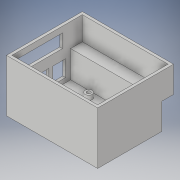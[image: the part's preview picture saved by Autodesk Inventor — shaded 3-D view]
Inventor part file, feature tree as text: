
AUTODESK INVENTOR PART (.ipt)
format: ipt  version: 2019.4 (Build 234330000, 330)  size: 207,872 bytes
history: native  units: mm
features: extrude x7, sketch x7
ambient origin geometry x8: Origin, YZ Plane, XZ Plane, XY Plane, X Axis, Y Axis, Z Axis, Center Point
bodies: Solid1 (feature_tree)
feature tree (14):
  extrude  "Extrusion1"  Depth=65.0mm
  extrude  "Extrusion2"  Depth=32.0mm TaperAngle=0.0deg
  extrude  "Extrusion3"  Depth=65.0mm
  extrude  "Extrusion4"  Depth=9.0mm
  extrude  "Extrusion5"  Depth=4.0mm
  extrude  "Extrusion6"  Depth=58.0mm
  extrude  "Extrusion7"  Depth=13.0mm
  sketch  "Sketch1"  dims[d0=95.0mm d1=65.0mm]
  sketch  "Sketch2"  dims[d2=3.0mm d3=32.0mm d4=0.0mm]
  sketch  "Sketch3"  dims[d5=95.0mm d6=65.0mm]
  sketch  "Sketch4"  dims[d7=30.0mm d8=0.0mm d9=9.0mm]
  sketch  "Sketch5"  dims[d10=10.0mm d11=4.0mm]
  sketch  "Sketch6"  dims[d12=8.0mm d13=20.0mm d15=49.0mm d16=20.0mm d18=58.0mm]
  sketch  "Sketch7"  dims[d21=5.0mm d22=0.0mm d23=13.0mm d24=3.0mm d25=0.0mm d26=100.0mm d27=3.0mm d28=3.0mm d29=84.0mm d30=3.0mm d31=84.0mm d32=100.0mm d33=3.0mm d34=26.0mm d35=0.0mm d36=9.142mm d37=6.5mm d38=50.0mm d39=15.0mm d40=5.0mm d41=90.0deg d42=5.54mm d43=14.0mm d44=18.0mm d45=4.5mm d46=14.0mm d47=18.0mm d48=3.0mm d49=0.0mm d50=1.0mm d51=5.0mm d52=27.75mm d53=8.0mm d54=4.0mm d55=3.0mm d56=0.0mm d62=101.0mm]
